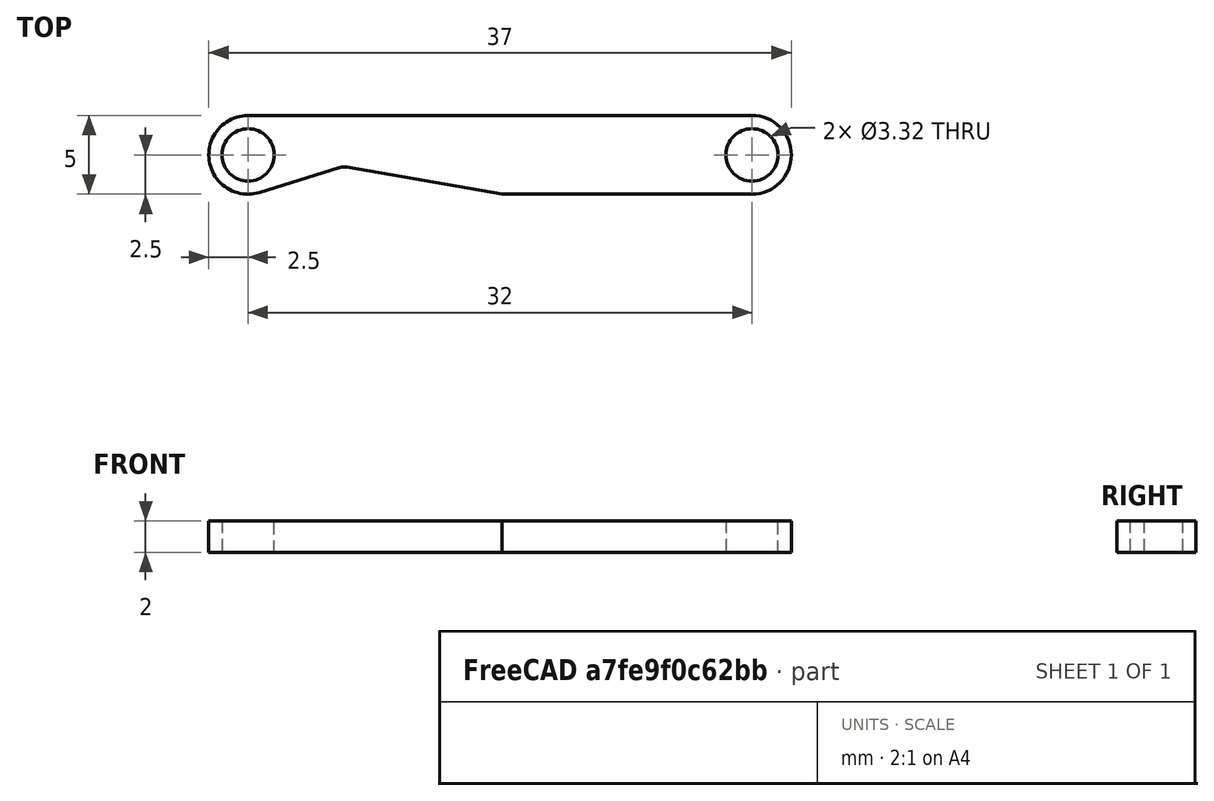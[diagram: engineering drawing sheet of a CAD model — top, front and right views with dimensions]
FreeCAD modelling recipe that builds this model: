
FCSTD DOCUMENT  (FreeCAD 1.0R39285 (Git))
Label: TransferLinkageLeft
License: All rights reserved
LicenseURL: https://en.wikipedia.org/wiki/All_rights_reserved
objects: Sketcher::SketchObject×1, App::Link×1, PartDesign::Pad×1, PartDesign::Body×1, App::Part×1
note: 6 computed .brp shape members not serialized (recipe doc carries the construction recipe); baked Part::Feature solids carry a one-line shape summary decoded from their .brp
EXTERNAL_REF file=../../Models/SteeringAckermannModel.FCStd obj=Spreadsheet

FEATURE [Sketcher::SketchObject] Sketch
  ArcFitTolerance = 1e-06
  AttachmentSupport = -> [XY_Plane001]
  FullyConstrained = true
  MakeInternals = false
  MapMode = 5
  expr: Constraints[4] = <<SteeringAckermannSpreadsheet>>.transferlinkagelength
  sketch-geometry (9):
    g0: Circle CenterX=0 CenterY=0 CenterZ=0 NormalX=0 NormalY=0 NormalZ=1 AngleXU=0 Radius=1.66
    g1: Circle CenterX=-32 CenterY=0 CenterZ=0 NormalX=0 NormalY=0 NormalZ=1 AngleXU=0 Radius=1.66
    g2: ArcOfCircle CenterX=0 CenterY=0 CenterZ=0 NormalX=0 NormalY=0 NormalZ=1 AngleXU=0 Radius=2.5 StartAngle=4.71239 EndAngle=7.85398
    g3: LineSegment StartX=8e-16 StartY=2.5 StartZ=0 EndX=-32 EndY=2.5 EndZ=0
    g4: LineSegment StartX=-5e-16 StartY=-2.5 StartZ=0 EndX=-15.88 EndY=-2.5 EndZ=0
    g5: ArcOfCircle CenterX=-32 CenterY=0 CenterZ=0 NormalX=0 NormalY=0 NormalZ=1 AngleXU=0 Radius=2.5 StartAngle=1.5708 EndAngle=5.01328
    g6: LineSegment StartX=-31.2591 StartY=-2.38768 StartZ=0 EndX=-26.1999 EndY=-0.817746 EndZ=0
    g7: ArcOfCircle CenterX=-25.9035 CenterY=-1.77282 CenterZ=0 NormalX=0 NormalY=0 NormalZ=1 AngleXU=0 Radius=1 StartAngle=1.39871 EndAngle=1.87169
    g8: LineSegment StartX=-25.7323 StartY=-0.787589 StartZ=0 EndX=-15.88 EndY=-2.5 EndZ=0
  constraints (21):
    c: Diameter(g0) = 3.32
    c: Coincident(g0,g-1)
    c: Diameter(g1) = 3.32
    c: PointOnObject(g1,g-1)
    c: DistanceX(g1,g0) = 32
    c: Coincident(g2,g0)
    c: Radius(g2) = 2.5
    c: Coincident(g5,g1)
    c: Tangent(g3,g2) = -1.5708
    c: Tangent(g4,g2) = 1.5708
    c: Tangent(g5,g3) = -1.5708
    c: Radius(g5) = 2.5
    c: Distance(g6,g6) = 5.29715
    c: Tangent(g6,g5) = -1.5708
    c: Radius(g7) = 1
    c: Tangent(g7,g6) = 1.5708
    c: Coincident(g8,g4)
    c: Distance(g8,g8) = 10
    c: Tangent(g8,g7) = 1.5708
    c: Parallel(g4,g3)
    c: DistanceX(g4,g4) = 15.88
FEATURE [App::Link] Link  label="SteeringAckermannSpreadsheet"
  LinkedObject = -> <external ../../Models/SteeringAckermannModel.FCStd>#Spreadsheet
FEATURE [PartDesign::Pad] Pad
  Direction = (0,0,1)
  Length = 2
  Length2 = 10
  Profile = -> Sketch
  ReferenceAxis = -> Sketch [N_Axis]
  Refine = true
  Suppressed = false
  Type = 0
FEATURE [PartDesign::Body] Body  label="TransferLinkageLeftBody"
  AllowCompound = false
  Group = -> [Sketch,Pad]
  Origin = -> Origin001
  Tip = -> Pad
FEATURE [App::Part] Part  label="TransferLinkageLeftPart"
  Group = -> [Body]
  Origin = -> Origin

RESOLVED EXTERNAL PARTS (link-assembly join: the EXTERNAL_REF files above that resolve inside this repo's crawl, each included once):
---- part ../../Models/SteeringAckermannModel.FCStd = doc fcstd_253a2b1971f8 ----
FCSTD DOCUMENT  (FreeCAD 1.0R39109 (Git))
Label: SteeringAckermannModel
License: All rights reserved
LicenseURL: https://en.wikipedia.org/wiki/All_rights_reserved
objects: Sketcher::SketchObject×2, Spreadsheet::Sheet×1, App::Part×1
note: 4 computed .brp shape members not serialized (recipe doc carries the construction recipe); baked Part::Feature solids carry a one-line shape summary decoded from their .brp

FEATURE [Sketcher::SketchObject] Sketch001  label="SteeringAckermannModel"
  ArcFitTolerance = 1e-06
  AttachmentSupport = -> [XY_Plane001]
  FullyConstrained = true
  MakeInternals = false
  MapMode = 5
  expr: .Constraints.BackTrackLength = <<SteeringAckermannSpreadsheet>>.track
  expr: .Constraints.LeftTransferLinkageLength = <<SteeringAckermannSpreadsheet>>.transferlinkagelength
  expr: .Constraints.LeftWheelDepth = <<SteeringAckermannSpreadsheet>>.wheeldepth
  expr: .Constraints.LeftWheelDiameter = <<SteeringAckermannSpreadsheet>>.wheeldia
  expr: .Constraints.LeftWheelLinkageAngle = <<SteeringAckermannSpreadsheet>>.wheellinkageangle
  expr: .Constraints.LeftWheelLinkageLength = <<SteeringAckermannSpreadsheet>>.wheellinkagelength
  expr: .Constraints.LeftWheelLinkageOffset = <<SteeringAckermannSpreadsheet>>.wheellinkageoffset
  expr: .Constraints.RightTransferLinkageLength = <<SteeringAckermannSpreadsheet>>.transferlinkagelength
  expr: .Constraints.RightWheelDepth = <<SteeringAckermannSpreadsheet>>.wheeldepth
  expr: .Constraints.RightWheelDiameter = <<SteeringAckermannSpreadsheet>>.wheeldia
  expr: .Constraints.RightWheelLinkageAngle = <<SteeringAckermannSpreadsheet>>.wheellinkageangle
  expr: .Constraints.RightWheelLinkageLength = <<SteeringAckermannSpreadsheet>>.wheellinkagelength
  expr: .Constraints.RightWheelLinkageOffset = <<SteeringAckermannSpreadsheet>>.wheellinkageoffset
  expr: .Constraints.ServoLinkageLength = <<SteeringAckermannSpreadsheet>>.servolinkagelength
  expr: .Constraints.ServoLinkageSeperation = <<SteeringAckermannSpreadsheet>>.servolinkagesep
  expr: .Constraints.ServoPositionOffset = <<SteeringAckermannSpreadsheet>>.servoposoffset
  expr: .Constraints.TrackAdj = Spreadsheet.trackadj
  expr: .Constraints.Wheelbase = <<SteeringAckermannSpreadsheet>>.wheelbase
  sketch-geometry (32):
    g0: LineSegment StartX=-34 StartY=0 StartZ=0 EndX=34 EndY=0 EndZ=0
    g1: LineSegment StartX=0 StartY=0 StartZ=0 EndX=0 EndY=-194 EndZ=0
    g2: GeomPoint [constr] X=0 Y=-4 Z=0
    g3: LineSegment StartX=0 StartY=-4 StartZ=0 EndX=8.69964 EndY=-12.2654 EndZ=0
    g4: LineSegment StartX=5.25574 StartY=-15.8902 StartZ=0 EndX=12.1435 EndY=-8.64052 EndZ=0
    g5: LineSegment StartX=5.25574 StartY=-15.8902 StartZ=0 EndX=-25.9767 EndY=-8.92334 EndZ=0
    g6: LineSegment StartX=-34 StartY=0 StartZ=0 EndX=-25.9767 EndY=-8.92334 EndZ=0
    g7: LineSegment StartX=-34 StartY=0 StartZ=0 EndX=-42.0301 EndY=-11.4681 EndZ=0
    g8: LineSegment StartX=12.1435 StartY=-8.64052 StartZ=0 EndX=44.0733 EndY=-6.5214 EndZ=0
    g9: LineSegment StartX=44.0733 StartY=-6.5214 StartZ=0 EndX=34 EndY=0 EndZ=0
    g10: LineSegment StartX=34 StartY=0 StartZ=0 EndX=44.0638 EndY=9.73246 EndZ=0
    g11: LineSegment StartX=-25.9767 StartY=-37.3581 StartZ=0 EndX=-71.8492 EndY=-5.23781 EndZ=0
    g12: LineSegment StartX=-71.8492 StartY=-5.23781 StartZ=0 EndX=-58.0834 EndY=14.4218 EndZ=0
    g13: LineSegment StartX=-58.0834 StartY=14.4218 StartZ=0 EndX=-12.2109 EndY=-17.6984 EndZ=0
    g14: LineSegment StartX=-12.2109 StartY=-17.6984 StartZ=0 EndX=-25.9767 EndY=-37.3581 EndZ=0
    g15: GeomPoint [constr] X=-42.0301 Y=-11.4681 Z=0
    g16: LineSegment StartX=54.9026 StartY=-18.7372 StartZ=0 EndX=15.9728 EndY=21.5179 EndZ=0
    g17: LineSegment StartX=15.9728 StartY=21.5179 StartZ=0 EndX=33.2249 EndY=38.2021 EndZ=0
    g18: LineSegment StartX=33.2249 StartY=38.2021 StartZ=0 EndX=72.1548 EndY=-2.05296 EndZ=0
    g19: LineSegment StartX=72.1548 StartY=-2.05296 StartZ=0 EndX=54.9026 EndY=-18.7372 EndZ=0
    g20: GeomPoint [constr] X=44.0638 Y=9.73246 Z=0
    g21: LineSegment StartX=-48 StartY=-194 StartZ=0 EndX=48 EndY=-194 EndZ=0
    g22: LineSegment StartX=-60 StartY=-222 StartZ=0 EndX=-60 EndY=-166 EndZ=0
    g23: LineSegment StartX=-60 StartY=-166 StartZ=0 EndX=-36 EndY=-166 EndZ=0
    g24: LineSegment StartX=-36 StartY=-166 StartZ=0 EndX=-36 EndY=-222 EndZ=0
    g25: LineSegment StartX=-36 StartY=-222 StartZ=0 EndX=-60 EndY=-222 EndZ=0
    g26: GeomPoint [constr] X=-48 Y=-194 Z=0
    g27: LineSegment StartX=36 StartY=-222 StartZ=0 EndX=36 EndY=-166 EndZ=0
    g28: LineSegment StartX=36 StartY=-166 StartZ=0 EndX=60 EndY=-166 EndZ=0
    g29: LineSegment StartX=60 StartY=-166 StartZ=0 EndX=60 EndY=-222 EndZ=0
    g30: LineSegment StartX=60 StartY=-222 StartZ=0 EndX=36 EndY=-222 EndZ=0
    g31: GeomPoint [constr] X=48 Y=-194 Z=0
  constraints (81):
    c: Distance(g1) = 194  'Wheelbase'
    c: Distance(g0) = 68  'TrackAdj'
    c: DistanceY(g1,g2) = -4  'ServoPositionOffset'
    c: Distance(g3) = 12  'ServoLinkageLength'
    c: Distance(g4) = 10  'ServoLinkageSeperation'
    c: Distance(g5) = 32  'LeftTransferLinkageLength'
    c: Distance(g6) = 12  'LeftWheelLinkageLength'
    c: Distance(g7) = 14  'LeftWheelLinkageOffset'
    c: Angle(g7,g6) = 1.34321  'LeftWheelLinkageAngle'
    c: Distance(g13) = 56  'LeftWheelDiameter'
    c: Distance(g14) = 24  'LeftWheelDepth'
    c: Distance(g8) = 32  'RightTransferLinkageLength'
    c: Distance(g9) = 12  'RightWheelLinkageLength'
    c: Distance(g10) = 14  'RightWheelLinkageOffset'
    c: Angle(g9,g10) = 1.34321  'RightWheelLinkageAngle'
    c: Distance(g16) = 56  'RightWheelDiameter'
    c: Distance(g19) = 24  'RightWheelDepth'
    c: Angle(g1,g3) = 0.810991  'SteeringAngle'
    c: Distance(g21) = 96  'BackTrackLength'
    c: Coincident(g5,g4)
    c: Horizontal(g0)
    c: Symmetric(g0,g0,g-1)
    c: Coincident(g1,g-1)
    c: PointOnObject(g1,g-2)
    c: PointOnObject(g2,g-2)
    c: Coincident(g3,g2)
    c: Perpendicular(g3,g4)
    c: Symmetric(g4,g4,g3)
    c: Coincident(g6,g0)
    c: Coincident(g6,g5)
    c: Coincident(g7,g0)
    c: Coincident(g8,g4)
    c: Coincident(g9,g8)
    c: Coincident(g9,g0)
    c: Coincident(g10,g0)
    c: Coincident(g11,g12)
    c: Coincident(g12,g13)
    c: Coincident(g13,g14)
    c: Coincident(g14,g11)
    c: Symmetric(g12,g11,g15)
    c: Coincident(g15,g7)
    c: Perpendicular(g13,g7)
    c: Perpendicular(g14,g13)
    c: Perpendicular(g12,g13)
    c: Perpendicular(g11,g7)
    c: Coincident(g16,g17)
    c: Coincident(g17,g18)
    c: Coincident(g18,g19)
    c: Coincident(g19,g16)
    c: Symmetric(g17,g16,g20)
    c: Coincident(g20,g10)
    c: Perpendicular(g16,g10)
    c: Perpendicular(g19,g16)
    c: Perpendicular(g17,g16)
    c: Perpendicular(g18,g10)
    c: Symmetric(g21,g21,g1)
    c: PointOnObject(g1,g21)
    c: Coincident(g22,g23)
    c: Coincident(g23,g24)
    c: Coincident(g24,g25)
    c: Coincident(g25,g22)
    c: Horizontal(g23)
    c: Horizontal(g25)
    c: Vertical(g22)
    c: Vertical(g24)
    c: Symmetric(g23,g22,g26)
    c: Coincident(g26,g21)
    c: Coincident(g27,g28)
    c: Coincident(g28,g29)
    c: Coincident(g29,g30)
    c: Coincident(g30,g27)
    c: Horizontal(g28)
    c: Horizontal(g30)
    c: Vertical(g27)
    c: Vertical(g29)
    c: Symmetric(g28,g27,g31)
    c: Coincident(g31,g21)
    c: Equal(g14,g25)
    c: Equal(g13,g24)
    c: Equal(g19,g30)
    c: Equal(g16,g27)
FEATURE [Spreadsheet::Sheet] Spreadsheet  label="SteeringAckermannSpreadsheet"
  cells = A1='CarDimension; B1='Value; C1='SteeringDimension; D1='Value; E1='CalculatedDimension; F1='Value; A2='BodyLength; B2=250; C2='ServoPositionOffset; D2(servoposoffset)=-4; E2='Wheelbase; F2(wheelbase)==B2 - B4; A3='BodyWidth; B3(bodywidth)=120; C3='ServoLinkageLength; D3(servolinkagelength)=12; E3='Track; F3(track)==B3 - B5; A4='WheelDiameter; B4(wheeldia)=56; C4='ServoLinkageTwoHoleSeperation; D4(servolinkagesep)=10; E4='TrackAdj; F4(trackadj)==F3 - D6 * 2; A5='WheelDepth; B5(wheeldepth)=24; C5='TransferLinkageLength; D5(transferlinkagelength)=32; C6='WheelLinkageOffset; D6(wheellinkageoffset)=14; C7='WheelLinkageLength; D7(wheellinkagelength)=12; C8='WheelLinkageAngle; D8(wheellinkageangle)=76.96
FEATURE [Sketcher::SketchObject] Sketch  label="SteeringAckermannModelLineOverlay"
  ArcFitTolerance = 1e-06
  AttachmentSupport = -> [XY_Plane001]
  ExternalGeometry = -> [Sketch001]
  FullyConstrained = true
  MakeInternals = false
  MapMode = 5
  sketch-geometry (3):
    g0: LineSegment StartX=-34 StartY=0 StartZ=0 EndX=-607.576 EndY=-819.152 EndZ=0
    g1: LineSegment StartX=44.0638 StartY=9.73246 StartZ=0 EndX=-674.776 EndY=-685.443 EndZ=0
    g2: LineSegment StartX=-500 StartY=-194 StartZ=0 EndX=500 EndY=-194 EndZ=0
  constraints (9):
    c: Coincident(g0,g-3)
    c: Coincident(g1,g-4)
    c: Horizontal(g2)
    c: Symmetric(g2,g2,g-5)
    c: Parallel(g-3,g0)
    c: Parallel(g-4,g1)
    c: Distance(g2) = 1000
    c: Distance(g1) = 1000
    c: Distance(g0) = 1000
FEATURE [App::Part] Part  label="SteeringAckermannModelPart-Abstact"
  Group = -> [Sketch001,Sketch]
  Origin = -> Origin001
